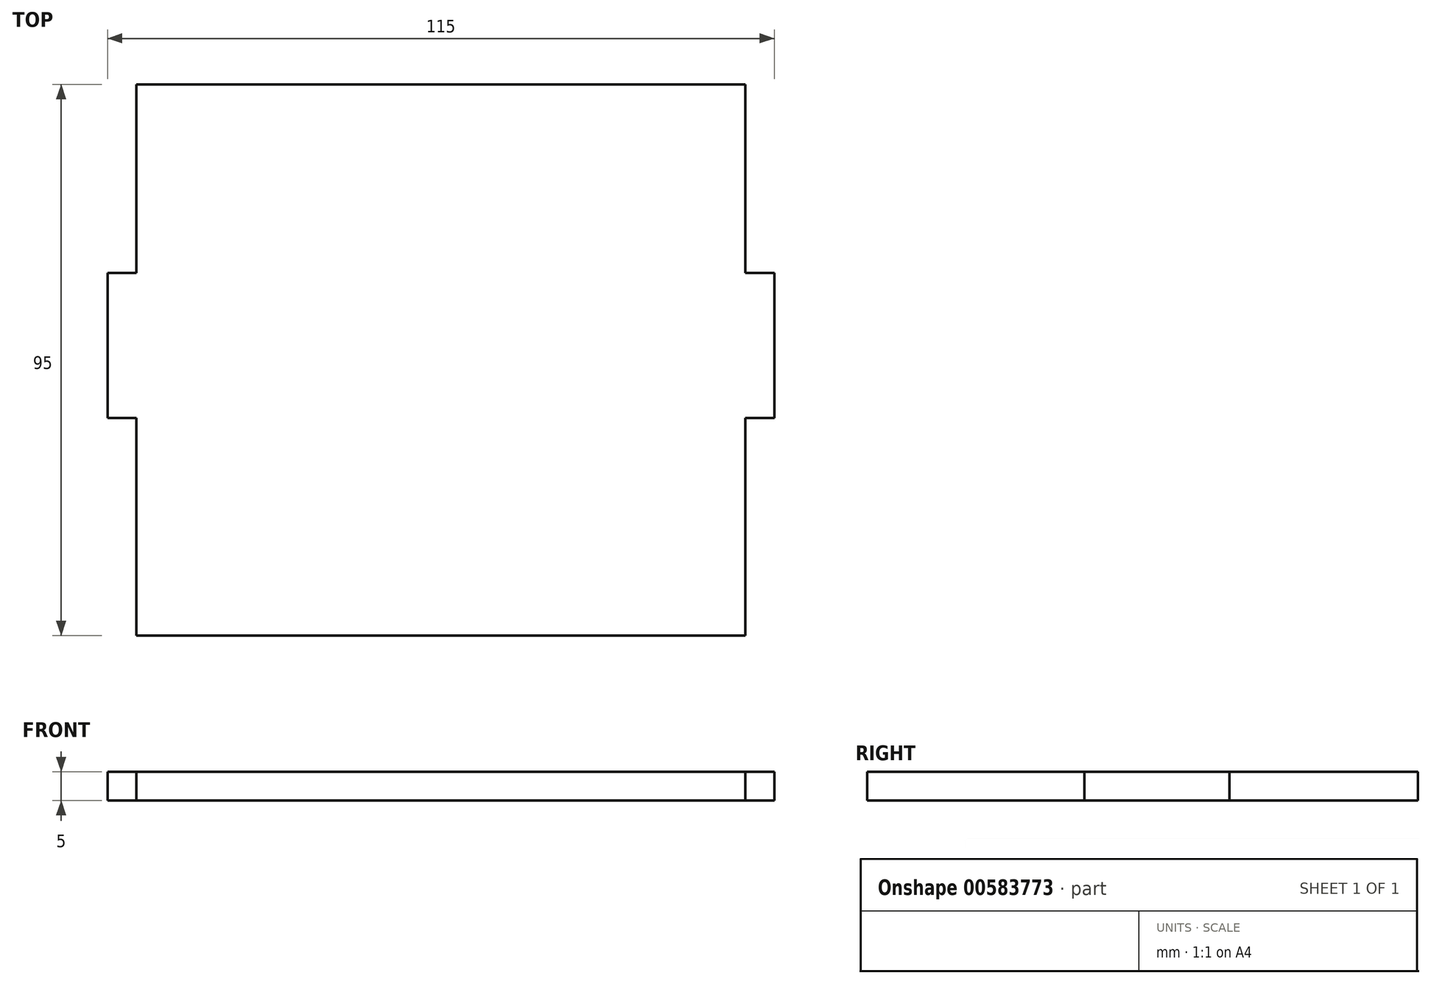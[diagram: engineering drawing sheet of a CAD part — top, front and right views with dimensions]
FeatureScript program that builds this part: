
annotation { "Feature Type Name" : "Feature", "Feature Type Description" : "" }
export const myFeature = defineFeature(function(context is Context, id is Id, definition is map)
    precondition{}
    {
        {
            var Q0;
            Q0=qCreatedBy(makeId("Top.planeOp"),FACE);
            var sketch = newSketch(context, id + "F0", { "sketchPlane" : qUnion([Q0])});
            skPoint(sketch, "E0.middle", {"position": v(-123.76, 80.46) * mm});
            skLineSegment(sketch, "E1.bottom", {"start": v(-52.5, -47.5) * mm, "end": v(52.5, -47.5) * mm});
            skLineSegment(sketch, "E1.top", {"start": v(-52.5, 47.5) * mm, "end": v(52.5, 47.5) * mm});
            skPoint(sketch, "E1.middle", {"position": v(0, 0) * mm});
            skLineSegment(sketch, "E2", {"start": v(52.5, 47.5) * mm, "end": v(52.5, 15) * mm});
            skLineSegment(sketch, "E3", {"start": v(52.5, 15) * mm, "end": v(57.5, 15) * mm});
            skLineSegment(sketch, "E4", {"start": v(57.5, 15) * mm, "end": v(57.5, -10) * mm});
            skLineSegment(sketch, "E5", {"start": v(57.5, -10) * mm, "end": v(52.5, -10) * mm});
            skLineSegment(sketch, "E6", {"start": v(52.5, -10) * mm, "end": v(52.5, -47.5) * mm});
            skLineSegment(sketch, "E7", {"start": v(-52.5, 47.5) * mm, "end": v(-52.5, 15) * mm});
            skLineSegment(sketch, "E8", {"start": v(-52.5, 15) * mm, "end": v(-57.5, 15) * mm});
            skLineSegment(sketch, "E9", {"start": v(-57.5, 15) * mm, "end": v(-57.5, -10) * mm});
            skLineSegment(sketch, "E10", {"start": v(-57.5, -10) * mm, "end": v(-52.5, -10) * mm});
            skLineSegment(sketch, "E11", {"start": v(-52.5, -10) * mm, "end": v(-52.5, -47.5) * mm});
            skSolve(sketch);
        }
        {
            var Q0;
            Q0 = qSketchRegion(id + "F0", true);
            extrude(context, id + "F1", {"entities" : qUnion([Q0]), "depth" : 5 * mm, "offsetDistance" : 25 * mm});
        }
    });
